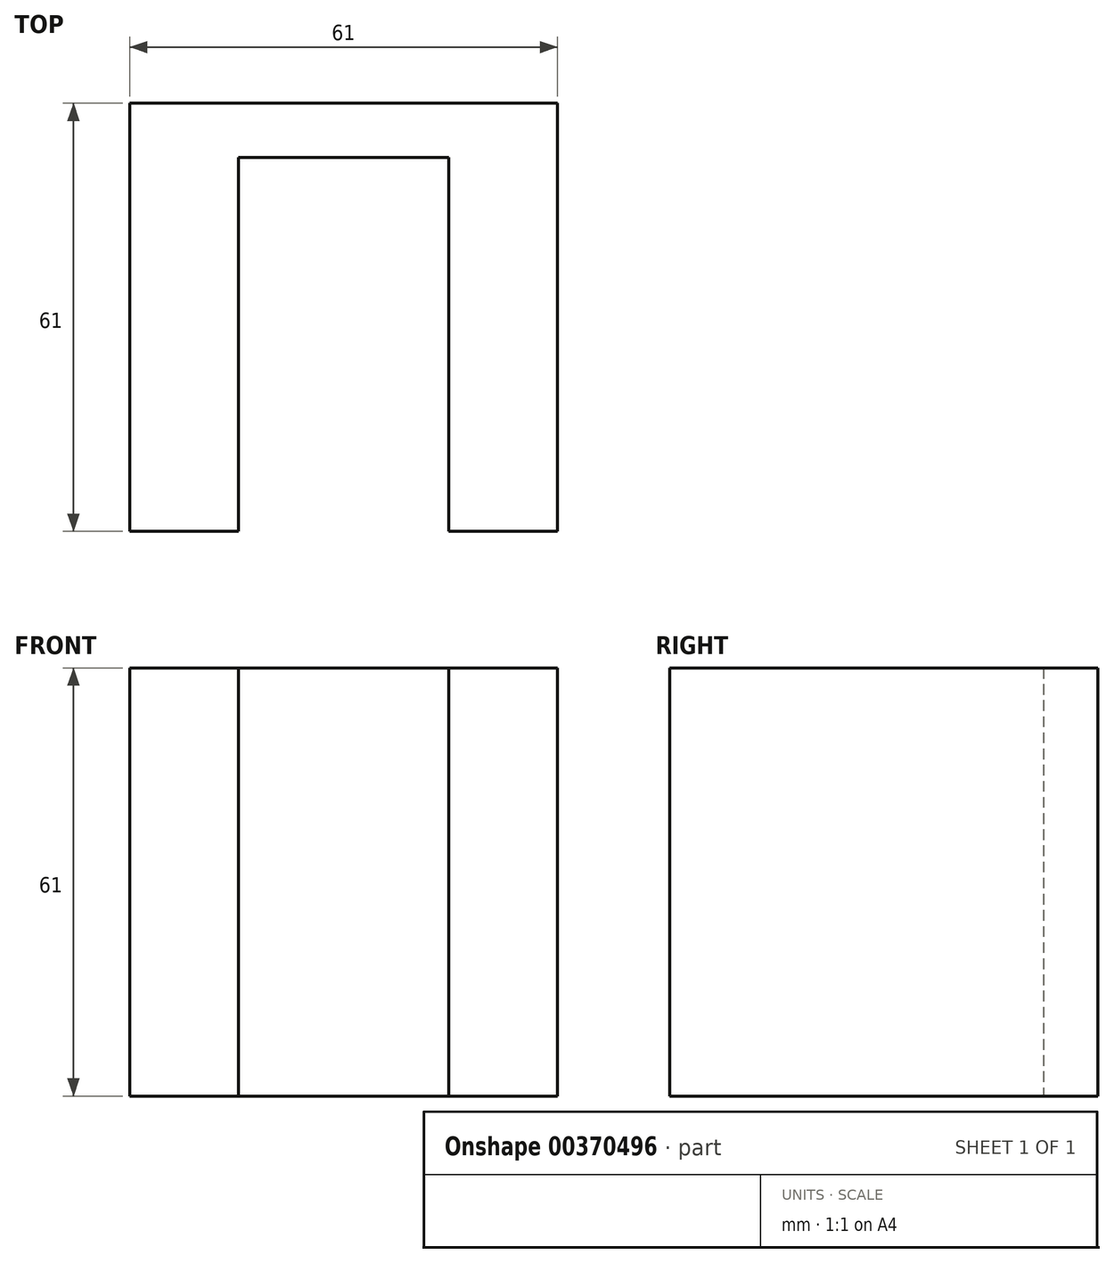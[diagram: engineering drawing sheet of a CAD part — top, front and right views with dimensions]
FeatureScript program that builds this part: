
annotation { "Feature Type Name" : "Feature", "Feature Type Description" : "" }
export const myFeature = defineFeature(function(context is Context, id is Id, definition is map)
    precondition{}
    {
        {
            var Q0;
            Q0=qCreatedBy(makeId("Top.planeOp"),FACE);
            var sketch = newSketch(context, id + "F0", { "sketchPlane" : qUnion([Q0])});
            skLineSegment(sketch, "E0", {"start": v(-23.13, -51.24) * mm, "end": v(-38.63, -51.24) * mm});
            skLineSegment(sketch, "E1", {"start": v(-38.63, -51.24) * mm, "end": v(-38.63, -8.24) * mm});
            skLineSegment(sketch, "E2", {"start": v(-38.63, 9.76) * mm, "end": v(22.37, 9.76) * mm});
            skLineSegment(sketch, "E3", {"start": v(22.37, -8.24) * mm, "end": v(22.37, -51.24) * mm});
            skLineSegment(sketch, "E4", {"start": v(22.37, -51.24) * mm, "end": v(6.87, -51.24) * mm});
            skLineSegment(sketch, "E5", {"start": v(6.87, -51.24) * mm, "end": v(6.87, 2) * mm});
            skLineSegment(sketch, "E6", {"start": v(6.87, 2) * mm, "end": v(-23.13, 2) * mm});
            skLineSegment(sketch, "E7", {"start": v(-23.13, 2) * mm, "end": v(-23.13, -51.24) * mm});
            skLineSegment(sketch, "E8", {"start": v(22.37, 9.76) * mm, "end": v(73.37, 9.76) * mm});
            skLineSegment(sketch, "E9", {"start": v(-38.63, 9.76) * mm, "end": v(-89.63, 9.76) * mm});
            skLineSegment(sketch, "E10", {"start": v(-89.63, -26.24) * mm, "end": v(-38.63, -26.24) * mm});
            skLineSegment(sketch, "E11", {"start": v(73.37, -26.24) * mm, "end": v(22.37, -26.24) * mm});
            skLineSegment(sketch, "E12", {"start": v(22.37, 9.76) * mm, "end": v(22.37, -8.24) * mm});
            skArc(sketch, "E13", {"start": v(-89.63, 9.76) * mm, "mid": v(-107.63, -8.24) * mm, "end": v(-89.63, -26.24) * mm});
            skArc(sketch, "E14", {"start": v(73.37, -26.24) * mm, "mid": v(91.37, -8.24) * mm, "end": v(73.37, 9.76) * mm});
            skLineSegment(sketch, "E15", {"start": v(-38.63, 9.76) * mm, "end": v(-38.63, -8.24) * mm});
            skCircle(sketch, "E16", {"center": v(-89.63, -8.24) * mm, "radius": 9.07 * mm});
            skCircle(sketch, "E17", {"center": v(73.37, -8.24) * mm, "radius": 9.1 * mm});
            skSolve(sketch);
        }
        {
            var Q0;
            {var subQ4=sQuery(id+"F0.wireOp",EDGE,"E0");Q0=makeQuery(id+"F0.imprint","IMPRINT",FACE,{"disambiguationData":[TD([[makeQuery(id+"F0.imprint","IMPRINT",EDGE,{"derivedFrom":subQ4}),-1.0]])]});}
            extrude(context, id + "F1", {"entities" : qUnion([Q0]), "depth" : 61 * mm});
        }
    });
